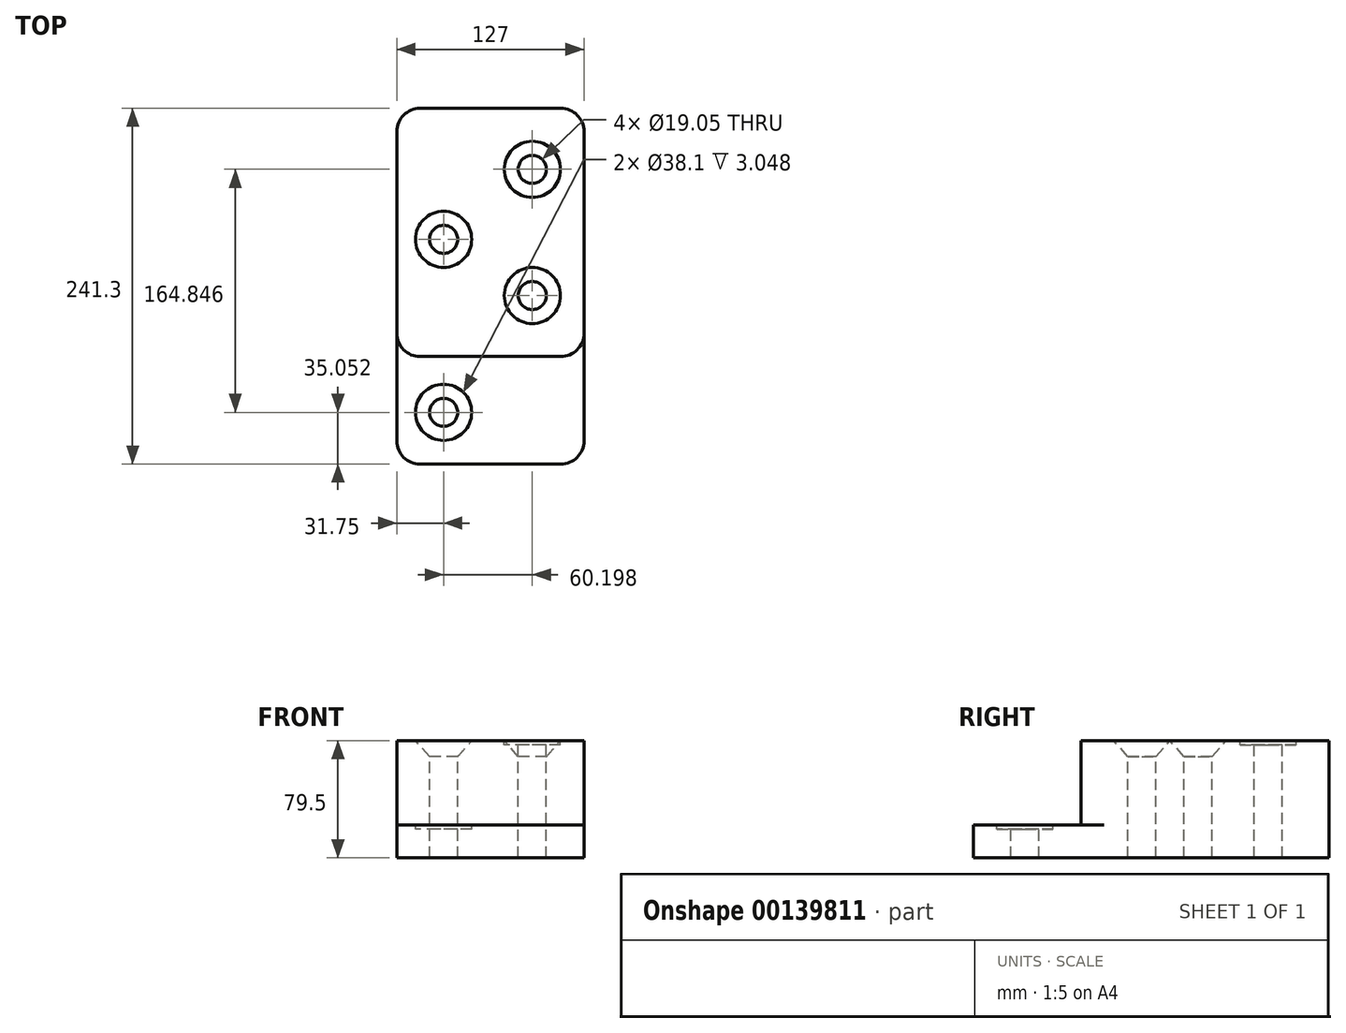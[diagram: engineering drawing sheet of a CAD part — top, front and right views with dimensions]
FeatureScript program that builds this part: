
annotation { "Feature Type Name" : "Feature", "Feature Type Description" : "" }
export const myFeature = defineFeature(function(context is Context, id is Id, definition is map)
    precondition{}
    {
        {
            var Q0;
            Q0=qCreatedBy(makeId("Top.planeOp"),FACE);
            var sketch = newSketch(context, id + "F0", { "sketchPlane" : qUnion([Q0])});
            skLineSegment(sketch, "E0.bottom", {"start": v(63.5, -120.65) * mm, "end": v(-63.5, -120.65) * mm});
            skLineSegment(sketch, "E0.top", {"start": v(63.5, 120.65) * mm, "end": v(-63.5, 120.65) * mm});
            skLineSegment(sketch, "E0.left", {"start": v(63.5, -120.65) * mm, "end": v(63.5, 120.65) * mm});
            skLineSegment(sketch, "E0.right", {"start": v(-63.5, -120.65) * mm, "end": v(-63.5, 120.65) * mm});
            skPoint(sketch, "E0.middle", {"position": v(0, 0) * mm});
            skSolve(sketch);
        }
        {
            var Q0;
            Q0 = qSketchRegion(id + "F0", true);
            extrude(context, id + "F1", {"entities" : qUnion([Q0]), "depth" : 22.35 * mm});
        }
        {
            var Q0;
            Q0=makeQuery(id+"F1.opExtrude","CAP_FACE",FACE,{"disambiguationData":[OSD([sQuery(id+"F0.wireOp",EDGE,"E0.bottom"),sQuery(id+"F0.wireOp",EDGE,"E0.top"),sQuery(id+"F0.wireOp",EDGE,"E0.left"),sQuery(id+"F0.wireOp",EDGE,"E0.right")])],"isStart":false});
            var sketch = newSketch(context, id + "F2", { "sketchPlane" : qUnion([Q0])});
            skLineSegment(sketch, "E1.bottom", {"start": v(-63.5, 120.65) * mm, "end": v(63.5, 120.65) * mm});
            skLineSegment(sketch, "E1.top", {"start": v(-63.5, -47.75) * mm, "end": v(63.5, -47.75) * mm});
            skLineSegment(sketch, "E1.left", {"start": v(-63.5, 120.65) * mm, "end": v(-63.5, -47.75) * mm});
            skLineSegment(sketch, "E1.right", {"start": v(63.5, 120.65) * mm, "end": v(63.5, -47.75) * mm});
            skSolve(sketch);
        }
        {
            var Q0;
            Q0 = qSketchRegion(id + "F2", true);
            extrude(context, id + "F3", {"entities" : qUnion([Q0]), "operationType" : NewBodyOperationType.ADD, "depth" : 57.15 * mm});
        }
        {
            var Q0;
            Q0=makeQuery(id+"F3.opExtrude","CAP_FACE",FACE,{"disambiguationData":[OSD([sQuery(id+"F2.wireOp",EDGE,"E1.bottom"),sQuery(id+"F2.wireOp",EDGE,"E1.top"),sQuery(id+"F2.wireOp",EDGE,"E1.left"),sQuery(id+"F2.wireOp",EDGE,"E1.right")])],"isStart":false});
            var sketch = newSketch(context, id + "F4", { "sketchPlane" : qUnion([Q0])});
            skLineSegment(sketch, "E2", {"start": v(63.5, 120.65) * mm, "end": v(28.45, 120.65) * mm, "construction": true});
            skLineSegment(sketch, "E3", {"start": v(28.45, 120.65) * mm, "end": v(28.45, 79.25) * mm, "construction": true});
            skLineSegment(sketch, "E4", {"start": v(28.45, 79.25) * mm, "end": v(28.45, -6.35) * mm, "construction": true});
            skLineSegment(sketch, "E5", {"start": v(63.5, 120.65) * mm, "end": v(-31.75, 120.65) * mm, "construction": true});
            skLineSegment(sketch, "E6", {"start": v(-31.75, 120.65) * mm, "end": v(-31.75, 31.75) * mm, "construction": true});
            skSolve(sketch);
        }
        {
            var Q0;
            Q0=sQuery(id+"F4.wireOp",VERTEX,"E6.end");
            var Q1;
            Q1=sQuery(id+"F4.wireOp",VERTEX,"E4.end");
            var Q2;
            Q2=makeQuery(id+"F1.opExtrude","SWEPT_BODY",BODY,{"disambiguationData":[OSD([sQuery(id+"F0.wireOp",EDGE,"E0.bottom"),sQuery(id+"F0.wireOp",EDGE,"E0.top"),sQuery(id+"F0.wireOp",EDGE,"E0.left"),sQuery(id+"F0.wireOp",EDGE,"E0.right")])]});
            hole(context, id + "F5", {"style" : HoleStyle.C_SINK, "endStyle" : HoleEndStyle.THROUGH, "holeDiameter" : 19.05 * mm, "cSinkDiameter" : 38.1 * mm, "cSinkAngle" : 82 * degree, "locations" : qUnion([Q0, Q1]), "scope" : qUnion([Q2]), "isTappedThrough" : true});
        }
        {
            var Q0;
            Q0=sQuery(id+"F4.wireOp",VERTEX,"E4.start");
            var Q1;
            Q1=makeQuery(id+"F1.opExtrude","SWEPT_BODY",BODY,{"disambiguationData":[OSD([sQuery(id+"F0.wireOp",EDGE,"E0.bottom"),sQuery(id+"F0.wireOp",EDGE,"E0.top"),sQuery(id+"F0.wireOp",EDGE,"E0.left"),sQuery(id+"F0.wireOp",EDGE,"E0.right")])]});
            hole(context, id + "F6", {"style" : HoleStyle.C_BORE, "endStyle" : HoleEndStyle.THROUGH, "holeDiameter" : 19.05 * mm, "cBoreDiameter" : 38.1 * mm, "cBoreDepth" : 3.05 * mm, "locations" : qUnion([Q0]), "scope" : qUnion([Q1]), "isTappedThrough" : true});
        }
        {
            var Q0;
            Q0=makeQuery(id+"F1.opExtrude","CAP_FACE",FACE,{"disambiguationData":[OSD([sQuery(id+"F0.wireOp",EDGE,"E0.bottom"),sQuery(id+"F0.wireOp",EDGE,"E0.top"),sQuery(id+"F0.wireOp",EDGE,"E0.left"),sQuery(id+"F0.wireOp",EDGE,"E0.right")])],"isStart":false});
            var sketch = newSketch(context, id + "F7", { "sketchPlane" : qUnion([Q0])});
            skLineSegment(sketch, "E7", {"start": v(63.5, -120.65) * mm, "end": v(-31.75, -120.65) * mm, "construction": true});
            skLineSegment(sketch, "E8", {"start": v(-31.75, -120.65) * mm, "end": v(-31.75, -85.6) * mm, "construction": true});
            skSolve(sketch);
        }
        {
            var Q0;
            Q0=sQuery(id+"F7.wireOp",VERTEX,"E8.end");
            var Q1;
            Q1=makeQuery(id+"F1.opExtrude","SWEPT_BODY",BODY,{"disambiguationData":[OSD([sQuery(id+"F0.wireOp",EDGE,"E0.bottom"),sQuery(id+"F0.wireOp",EDGE,"E0.top"),sQuery(id+"F0.wireOp",EDGE,"E0.left"),sQuery(id+"F0.wireOp",EDGE,"E0.right")])]});
            hole(context, id + "F8", {"style" : HoleStyle.C_BORE, "endStyle" : HoleEndStyle.THROUGH, "holeDiameter" : 19.05 * mm, "cBoreDiameter" : 38.1 * mm, "cBoreDepth" : 3.05 * mm, "locations" : qUnion([Q0]), "scope" : qUnion([Q1]), "isTappedThrough" : true});
        }
        {
            var Q0;
            Q0=makeQuery(id+"F3.opExtrude","SWEPT_EDGE",EDGE,{"disambiguationData":[OSD([sQuery(id+"F0.wireOp",EDGE,"E0.left"),sQuery(id+"F2.wireOp",EDGE,"E1.top"),sQuery(id+"F2.wireOp",EDGE,"E1.right")])]});
            var Q1;
            Q1=makeQuery(id+"F3.opExtrude","SWEPT_EDGE",EDGE,{"disambiguationData":[OSD([sQuery(id+"F0.wireOp",EDGE,"E0.right"),sQuery(id+"F2.wireOp",EDGE,"E1.top"),sQuery(id+"F2.wireOp",EDGE,"E1.left")])]});
            var Q2;
            Q2=makeQuery(id+"F1.opExtrude","SWEPT_EDGE",EDGE,{"disambiguationData":[OSD([sQuery(id+"F0.wireOp",EDGE,"E0.bottom"),sQuery(id+"F0.wireOp",EDGE,"E0.right")])]});
            var Q3;
            Q3=makeQuery(id+"F1.opExtrude","SWEPT_EDGE",EDGE,{"disambiguationData":[OSD([sQuery(id+"F0.wireOp",EDGE,"E0.bottom"),sQuery(id+"F0.wireOp",EDGE,"E0.left")])]});
            var Q4;
            Q4=makeQuery(id+"F3.boolean.opBoolean","MERGE",EDGE,{"derivedFrom":[makeQuery(id+"F1.opExtrude","SWEPT_EDGE",EDGE,{"disambiguationData":[OSD([sQuery(id+"F0.wireOp",EDGE,"E0.top"),sQuery(id+"F0.wireOp",EDGE,"E0.left")])]}),makeQuery(id+"F3.opExtrude","SWEPT_EDGE",EDGE,{"disambiguationData":[OSD([sQuery(id+"F2.wireOp",EDGE,"E1.bottom"),sQuery(id+"F2.wireOp",EDGE,"E1.right")])]})]});
            var Q5;
            Q5=makeQuery(id+"F3.boolean.opBoolean","MERGE",EDGE,{"derivedFrom":[makeQuery(id+"F1.opExtrude","SWEPT_EDGE",EDGE,{"disambiguationData":[OSD([sQuery(id+"F0.wireOp",EDGE,"E0.top"),sQuery(id+"F0.wireOp",EDGE,"E0.right")])]}),makeQuery(id+"F3.opExtrude","SWEPT_EDGE",EDGE,{"disambiguationData":[OSD([sQuery(id+"F2.wireOp",EDGE,"E1.bottom"),sQuery(id+"F2.wireOp",EDGE,"E1.left")])]})]});
            fillet(context, id + "F9", {"entities" : qUnion([Q0, Q1, Q2, Q3, Q4, Q5]), "radius" : 15.75 * mm, "tangentPropagation" : true, "allowEdgeOverflow" : false});
        }
    });
